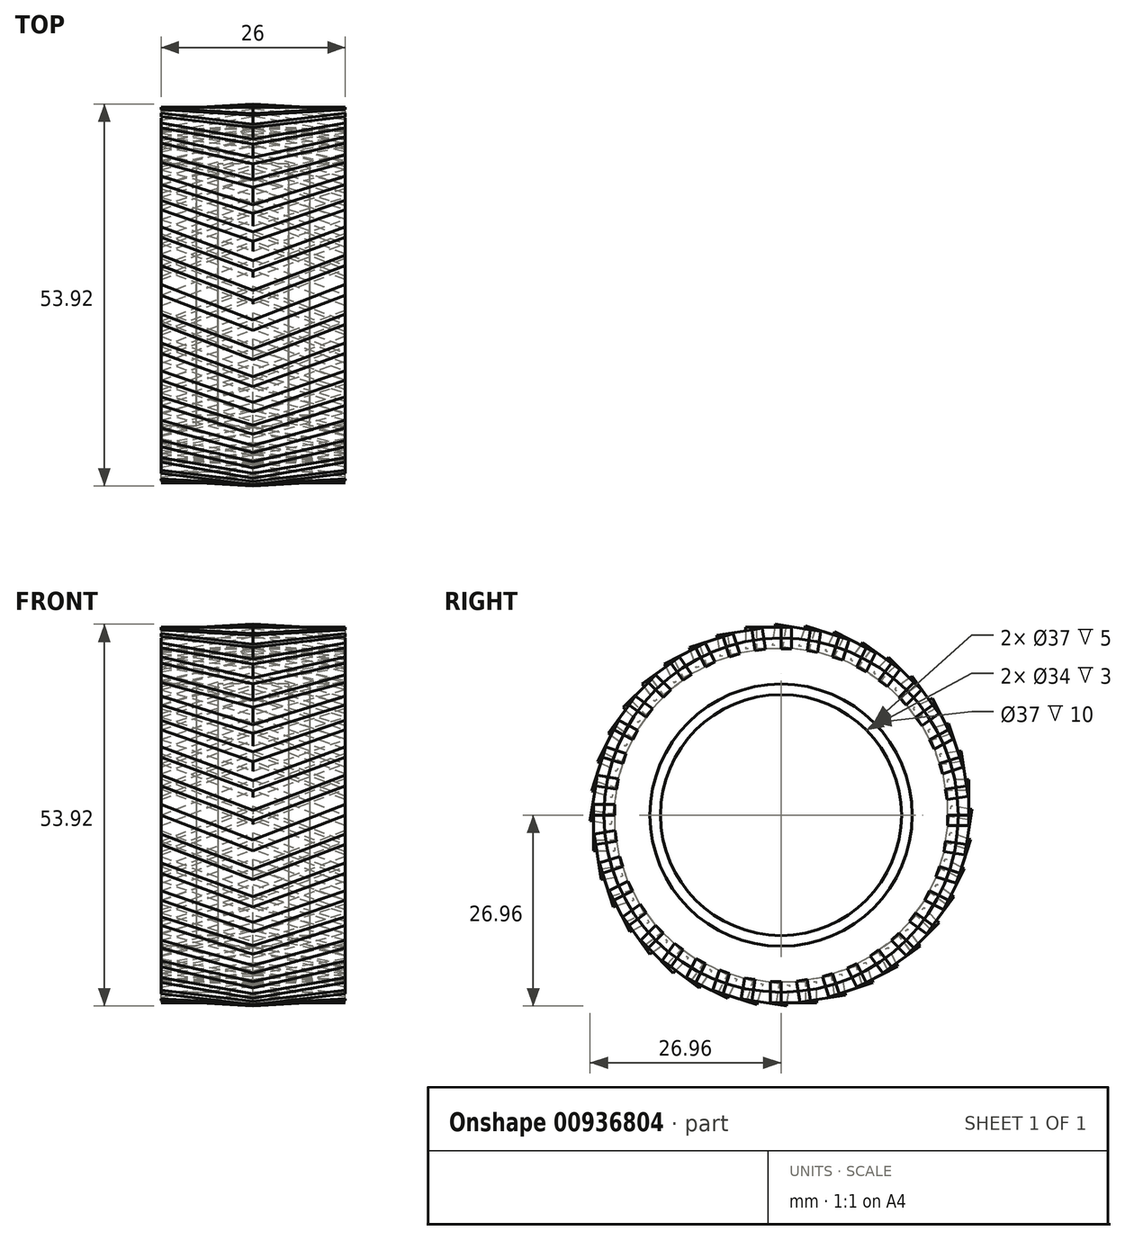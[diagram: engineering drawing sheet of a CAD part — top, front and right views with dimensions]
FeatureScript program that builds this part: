
annotation { "Feature Type Name" : "Feature", "Feature Type Description" : "" }
export const myFeature = defineFeature(function(context is Context, id is Id, definition is map)
    precondition{}
    {
        {
            var Q0;
            Q0=qCreatedBy(makeId("Front.planeOp"),FACE);
            var sketch = newSketch(context, id + "F0", { "sketchPlane" : qUnion([Q0])});
            skLineSegment(sketch, "E0", {"start": v(-5, 18.5) * mm, "end": v(-5, 17) * mm});
            skLineSegment(sketch, "E1", {"start": v(-5, 17) * mm, "end": v(-8, 17) * mm});
            skLineSegment(sketch, "E2", {"start": v(-8, 17) * mm, "end": v(-8, 18.5) * mm});
            skLineSegment(sketch, "E3", {"start": v(-8, 18.5) * mm, "end": v(-13, 18.5) * mm});
            skLineSegment(sketch, "E4", {"start": v(-13, 18.5) * mm, "end": v(-13, 25) * mm});
            skLineSegment(sketch, "E5.MirrorCS", {"start": v(5, 18.5) * mm, "end": v(5, 17) * mm});
            skLineSegment(sketch, "E6.MirrorCS", {"start": v(8, 17) * mm, "end": v(8, 18.5) * mm});
            skLineSegment(sketch, "E7.MirrorCS", {"start": v(13, 18.5) * mm, "end": v(13, 25) * mm});
            skLineSegment(sketch, "E8.MirrorCS", {"start": v(8, 18.5) * mm, "end": v(13, 18.5) * mm});
            skLineSegment(sketch, "E9.MirrorCS", {"start": v(5, 17) * mm, "end": v(8, 17) * mm});
            skLineSegment(sketch, "E10", {"start": v(-13, 0) * mm, "end": v(13, 0) * mm});
            skLineSegment(sketch, "E11", {"start": v(-13, 25) * mm, "end": v(13, 25) * mm});
            skLineSegment(sketch, "E12", {"start": v(-5, 18.5) * mm, "end": v(5, 18.5) * mm});
            skSolve(sketch);
        }
        {
            var Q0;
            Q0=makeQuery(id+"F0.imprint","IMPRINT",FACE,{"disambiguationData":[TD([[makeQuery(id+"F0.imprint","IMPRINT",EDGE,{"derivedFrom":sQuery(id+"F0.wireOp",EDGE,"E0")}),-1.0]])]});
            var Q1;
            Q1=sQuery(id+"F0.wireOp",EDGE,"E10");
            revolve(context, id + "F1", {"surfaceOperationType" : NewSurfaceOperationType.NEW, "entities" : qUnion([Q0]), "axis" : qUnion([Q1]), "revolveType" : RevolveType.FULL});
        }
        {
            var Q0;
            Q0=qCreatedBy(makeId("Top.planeOp"),FACE);
            var sketch = newSketch(context, id + "F2", { "sketchPlane" : qUnion([Q0])});
            skLineSegment(sketch, "E13", {"start": v(-13, 0) * mm, "end": v(0, -5) * mm});
            skLineSegment(sketch, "E14", {"start": v(0, -5) * mm, "end": v(13, 0) * mm});
            skLineSegment(sketch, "E15", {"start": v(0, -5) * mm, "end": v(0, -3.5) * mm, "construction": true});
            skLineSegment(sketch, "E16", {"start": v(-13, 1.5) * mm, "end": v(-13, 0) * mm});
            skLineSegment(sketch, "E17", {"start": v(13, 1.5) * mm, "end": v(13, 0) * mm});
            skLineSegment(sketch, "E18", {"start": v(-13, 1.5) * mm, "end": v(0, -3.5) * mm});
            skLineSegment(sketch, "E19", {"start": v(13, 1.5) * mm, "end": v(0, -3.5) * mm});
            skSolve(sketch);
        }
        {
            var Q0;
            Q0=makeQuery(id+"F2.imprint","IMPRINT",FACE,{"disambiguationData":[TD([[makeQuery(id+"F2.imprint","IMPRINT",EDGE,{"derivedFrom":sQuery(id+"F2.wireOp",EDGE,"E13")}),1.0]])]});
            extrude(context, id + "F3", {"entities" : qUnion([Q0]), "depth" : 26.5 * mm, "offsetDistance" : 25 * mm, "hasSecondDirection" : true, "secondDirectionOppositeDirection" : false, "secondDirectionDepth" : 23.5 * mm});
        }
        {
            var Q0;
            Q0=makeQuery(id+"F3.opExtrude","SWEPT_BODY",BODY,{"disambiguationData":[OSD([sQuery(id+"F2.wireOp",EDGE,"E13"),sQuery(id+"F2.wireOp",EDGE,"E14"),sQuery(id+"F2.wireOp",EDGE,"fac9cc86-7357-45ef-9a00-561bb5577302"),sQuery(id+"F2.wireOp",EDGE,"c3d3e2a7-585d-44c0-b52b-73053a58dc2e"),sQuery(id+"F2.wireOp",EDGE,"E16"),sQuery(id+"F2.wireOp",EDGE,"E17")])]});
            var Q1;
            Q1=sQuery(id+"F0.wireOp",EDGE,"E10");
            circularPattern(context, id + "F4", {"entities" : qUnion([Q0]), "axis" : qUnion([Q1]), "angle" : 360 * degree, "instanceCount" : 40, "equalSpace" : true});
        }
    });
